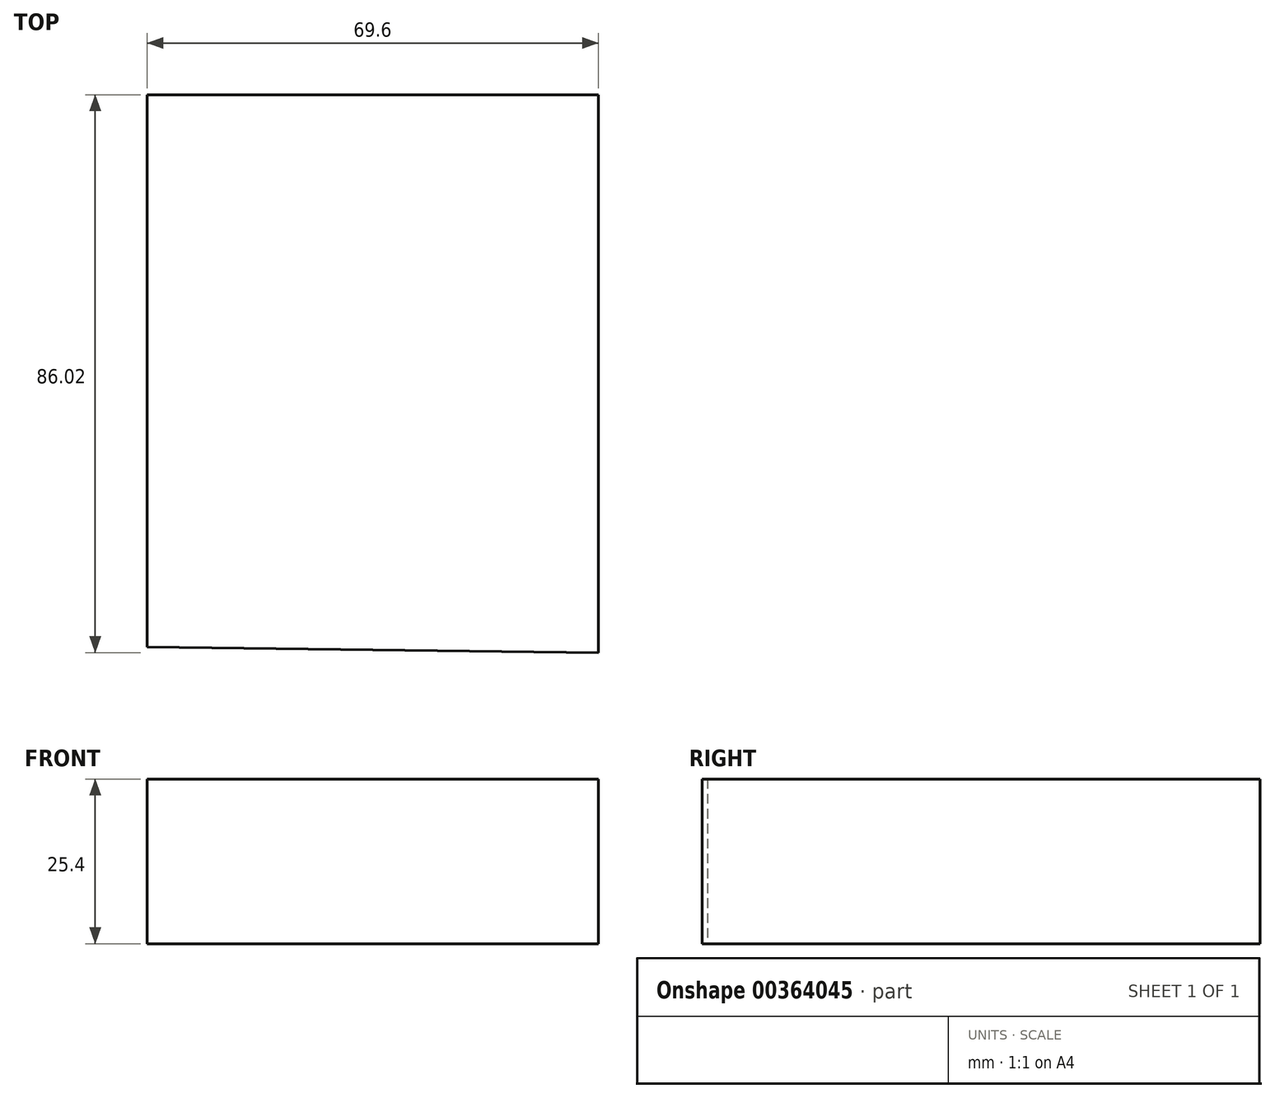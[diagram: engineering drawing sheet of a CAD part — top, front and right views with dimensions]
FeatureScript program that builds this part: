
annotation { "Feature Type Name" : "Feature", "Feature Type Description" : "" }
export const myFeature = defineFeature(function(context is Context, id is Id, definition is map)
    precondition{}
    {
        {
            var Q0;
            Q0=qCreatedBy(makeId("Top.planeOp"),FACE);
            var sketch = newSketch(context, id + "F0", { "sketchPlane" : qUnion([Q0])});
            skLineSegment(sketch, "E0", {"start": v(-40.47, -35.8) * mm, "end": v(-40.47, 49.38) * mm});
            skLineSegment(sketch, "E1", {"start": v(-40.47, 49.38) * mm, "end": v(29.13, 49.38) * mm});
            skLineSegment(sketch, "E2", {"start": v(29.13, 49.38) * mm, "end": v(29.13, -36.64) * mm});
            skLineSegment(sketch, "E3", {"start": v(29.13, -36.64) * mm, "end": v(-40.47, -35.8) * mm});
            skSolve(sketch);
        }
        {
            var Q0;
            Q0 = qSketchRegion(id + "F0", true);
            extrude(context, id + "F1", {"entities" : qUnion([Q0]), "depth" : 25.4 * mm});
        }
    });
